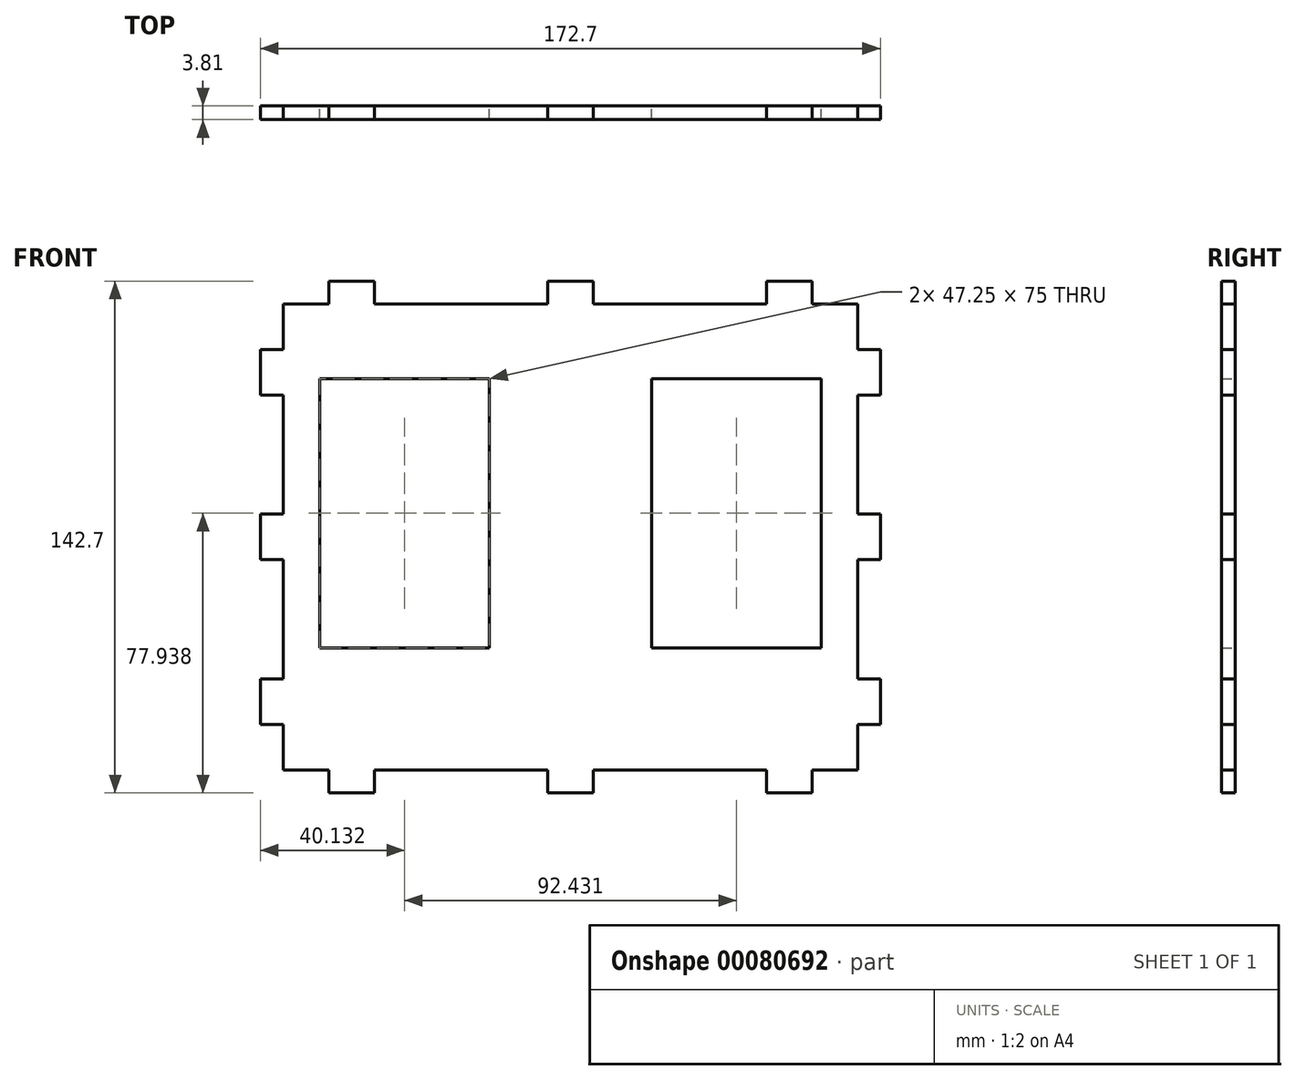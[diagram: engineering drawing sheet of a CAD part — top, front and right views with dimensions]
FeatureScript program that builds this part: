
annotation { "Feature Type Name" : "Feature", "Feature Type Description" : "" }
export const myFeature = defineFeature(function(context is Context, id is Id, definition is map)
    precondition{}
    {
        {
            var Q0;
            Q0=qCreatedBy(makeId("Front.planeOp"),FACE);
            var sketch = newSketch(context, id + "F0", { "sketchPlane" : qUnion([Q0])});
            skLineSegment(sketch, "E0.bottom", {"start": v(-197.85, -61.57) * mm, "end": v(-357.85, -61.57) * mm});
            skLineSegment(sketch, "E0.top", {"start": v(-197.85, 68.43) * mm, "end": v(-357.85, 68.43) * mm});
            skLineSegment(sketch, "E0.left", {"start": v(-197.85, -61.57) * mm, "end": v(-197.85, 68.43) * mm});
            skLineSegment(sketch, "E0.right", {"start": v(-357.85, -61.57) * mm, "end": v(-357.85, 68.43) * mm});
            skPoint(sketch, "E0.middle", {"position": v(-277.85, 3.43) * mm});
            skLineSegment(sketch, "E1.bottom", {"start": v(-271.5, 74.78) * mm, "end": v(-284.2, 74.78) * mm});
            skLineSegment(sketch, "E1.top", {"start": v(-271.5, 62.08) * mm, "end": v(-284.2, 62.08) * mm});
            skLineSegment(sketch, "E1.left", {"start": v(-271.5, 74.78) * mm, "end": v(-271.5, 62.08) * mm});
            skLineSegment(sketch, "E1.right", {"start": v(-284.2, 74.78) * mm, "end": v(-284.2, 62.08) * mm});
            skPoint(sketch, "E1.middle", {"position": v(-277.85, 68.43) * mm});
            skLineSegment(sketch, "E2.bottom", {"start": v(-223.25, 74.78) * mm, "end": v(-210.55, 74.78) * mm});
            skLineSegment(sketch, "E2.top", {"start": v(-223.25, 62.08) * mm, "end": v(-210.55, 62.08) * mm});
            skLineSegment(sketch, "E2.left", {"start": v(-223.25, 74.78) * mm, "end": v(-223.25, 62.08) * mm});
            skLineSegment(sketch, "E2.right", {"start": v(-210.55, 74.78) * mm, "end": v(-210.55, 62.08) * mm});
            skPoint(sketch, "E2.middle", {"position": v(-216.9, 68.43) * mm});
            skLineSegment(sketch, "E3.bottom", {"start": v(-332.45, 74.78) * mm, "end": v(-345.15, 74.78) * mm});
            skLineSegment(sketch, "E3.top", {"start": v(-332.45, 62.08) * mm, "end": v(-345.15, 62.08) * mm});
            skLineSegment(sketch, "E3.left", {"start": v(-332.45, 74.78) * mm, "end": v(-332.45, 62.08) * mm});
            skLineSegment(sketch, "E3.right", {"start": v(-345.15, 74.78) * mm, "end": v(-345.15, 62.08) * mm});
            skPoint(sketch, "E3.middle", {"position": v(-338.8, 68.43) * mm});
            skLineSegment(sketch, "E4.bottom", {"start": v(-364.2, 9.78) * mm, "end": v(-351.5, 9.78) * mm});
            skLineSegment(sketch, "E4.top", {"start": v(-364.2, -2.92) * mm, "end": v(-351.5, -2.92) * mm});
            skLineSegment(sketch, "E4.left", {"start": v(-364.2, 9.78) * mm, "end": v(-364.2, -2.92) * mm});
            skLineSegment(sketch, "E4.right", {"start": v(-351.5, 9.78) * mm, "end": v(-351.5, -2.92) * mm});
            skPoint(sketch, "E4.middle", {"position": v(-357.85, 3.43) * mm});
            skLineSegment(sketch, "E5.bottom", {"start": v(-364.2, 55.73) * mm, "end": v(-351.5, 55.73) * mm});
            skLineSegment(sketch, "E5.top", {"start": v(-364.2, 43.03) * mm, "end": v(-351.5, 43.03) * mm});
            skLineSegment(sketch, "E5.left", {"start": v(-364.2, 55.73) * mm, "end": v(-364.2, 43.03) * mm});
            skLineSegment(sketch, "E5.right", {"start": v(-351.5, 55.73) * mm, "end": v(-351.5, 43.03) * mm});
            skPoint(sketch, "E5.middle", {"position": v(-357.85, 49.38) * mm});
            skLineSegment(sketch, "E6.bottom", {"start": v(-347.7, 47.52) * mm, "end": v(-300.44, 47.52) * mm});
            skLineSegment(sketch, "E6.top", {"start": v(-347.7, -27.48) * mm, "end": v(-300.44, -27.48) * mm});
            skLineSegment(sketch, "E6.left", {"start": v(-347.7, 47.52) * mm, "end": v(-347.7, -27.48) * mm});
            skLineSegment(sketch, "E6.right", {"start": v(-300.44, 47.52) * mm, "end": v(-300.44, -27.48) * mm});
            skLineSegment(sketch, "E7", {"start": v(-277.85, 68.43) * mm, "end": v(-277.85, -61.57) * mm});
            skLineSegment(sketch, "E8.MirrorCS", {"start": v(-255.26, 47.52) * mm, "end": v(-255.26, -27.48) * mm});
            skLineSegment(sketch, "E9.MirrorCS", {"start": v(-208.01, 47.52) * mm, "end": v(-255.26, 47.52) * mm});
            skLineSegment(sketch, "E10.MirrorCS", {"start": v(-208.01, 47.52) * mm, "end": v(-208.01, -27.48) * mm});
            skLineSegment(sketch, "E11.MirrorCS", {"start": v(-208.01, -27.48) * mm, "end": v(-255.26, -27.48) * mm});
            skLineSegment(sketch, "E12.MirrorCS", {"start": v(-271.5, -55.22) * mm, "end": v(-284.2, -55.22) * mm});
            skLineSegment(sketch, "E13.MirrorCS", {"start": v(-284.2, -67.92) * mm, "end": v(-284.2, -55.22) * mm});
            skLineSegment(sketch, "E14.MirrorCS", {"start": v(-271.5, -67.92) * mm, "end": v(-284.2, -67.92) * mm});
            skLineSegment(sketch, "E15.MirrorCS", {"start": v(-271.5, -67.92) * mm, "end": v(-271.5, -55.22) * mm});
            skLineSegment(sketch, "E16.MirrorCS", {"start": v(-223.25, -67.92) * mm, "end": v(-223.25, -55.22) * mm});
            skLineSegment(sketch, "E17.MirrorCS", {"start": v(-223.25, -67.92) * mm, "end": v(-210.55, -67.92) * mm});
            skLineSegment(sketch, "E18.MirrorCS", {"start": v(-210.55, -67.92) * mm, "end": v(-210.55, -55.22) * mm});
            skLineSegment(sketch, "E19.MirrorCS", {"start": v(-223.25, -55.22) * mm, "end": v(-210.55, -55.22) * mm});
            skLineSegment(sketch, "E20.MirrorCS", {"start": v(-332.45, -55.22) * mm, "end": v(-345.15, -55.22) * mm});
            skLineSegment(sketch, "E21.MirrorCS", {"start": v(-332.45, -67.92) * mm, "end": v(-332.45, -55.22) * mm});
            skLineSegment(sketch, "E22.MirrorCS", {"start": v(-332.45, -67.92) * mm, "end": v(-345.15, -67.92) * mm});
            skLineSegment(sketch, "E23.MirrorCS", {"start": v(-345.15, -67.92) * mm, "end": v(-345.15, -55.22) * mm});
            skLineSegment(sketch, "E24.bottom", {"start": v(-364.2, -36.17) * mm, "end": v(-351.5, -36.17) * mm});
            skLineSegment(sketch, "E24.top", {"start": v(-364.2, -48.87) * mm, "end": v(-351.5, -48.87) * mm});
            skLineSegment(sketch, "E24.left", {"start": v(-364.2, -36.17) * mm, "end": v(-364.2, -48.87) * mm});
            skLineSegment(sketch, "E24.right", {"start": v(-351.5, -36.17) * mm, "end": v(-351.5, -48.87) * mm});
            skPoint(sketch, "E24.middle", {"position": v(-357.85, -42.52) * mm});
            skLineSegment(sketch, "E25.MirrorCS", {"start": v(-204.2, -36.17) * mm, "end": v(-204.2, -48.87) * mm});
            skLineSegment(sketch, "E26.MirrorCS", {"start": v(-191.5, -36.17) * mm, "end": v(-204.2, -36.17) * mm});
            skLineSegment(sketch, "E27.MirrorCS", {"start": v(-191.5, -36.17) * mm, "end": v(-191.5, -48.87) * mm});
            skLineSegment(sketch, "E28.MirrorCS", {"start": v(-191.5, -48.87) * mm, "end": v(-204.2, -48.87) * mm});
            skLineSegment(sketch, "E29.MirrorCS", {"start": v(-191.5, -2.92) * mm, "end": v(-204.2, -2.92) * mm});
            skLineSegment(sketch, "E30.MirrorCS", {"start": v(-204.2, 9.78) * mm, "end": v(-204.2, -2.92) * mm});
            skLineSegment(sketch, "E31.MirrorCS", {"start": v(-191.5, 9.78) * mm, "end": v(-204.2, 9.78) * mm});
            skLineSegment(sketch, "E32.MirrorCS", {"start": v(-191.5, 9.78) * mm, "end": v(-191.5, -2.92) * mm});
            skLineSegment(sketch, "E33.MirrorCS", {"start": v(-191.5, 43.03) * mm, "end": v(-204.2, 43.03) * mm});
            skLineSegment(sketch, "E34.MirrorCS", {"start": v(-191.5, 55.73) * mm, "end": v(-204.2, 55.73) * mm});
            skLineSegment(sketch, "E35.MirrorCS", {"start": v(-204.2, 55.73) * mm, "end": v(-204.2, 43.03) * mm});
            skLineSegment(sketch, "E36.MirrorCS", {"start": v(-191.5, 55.73) * mm, "end": v(-191.5, 43.03) * mm});
            skPoint(sketch, "E37.trimOffspring.end.orphan", {"position": v(-197.85, 3.43) * mm});
            skSolve(sketch);
        }
        {
            var Q0;
            {var subQ5=sQuery(id+"F0.wireOp",EDGE,"E5.right");Q0=makeQuery(id+"F0.imprint","IMPRINT",FACE,{"disambiguationData":[TD([[makeQuery(id+"F0.imprint","IMPRINT",EDGE,{"derivedFrom":subQ5}),-1.0]])]});}
            var Q1;
            {var subQ5=sQuery(id+"F0.wireOp",EDGE,"E5.left");Q1=makeQuery(id+"F0.imprint","IMPRINT",FACE,{"disambiguationData":[TD([[makeQuery(id+"F0.imprint","IMPRINT",EDGE,{"derivedFrom":subQ5}),1.0]])]});}
            var Q2;
            {var subQ0=sQuery(id+"F0.wireOp",EDGE,"E0.right");var subQ1=sQuery(id+"F0.wireOp",EDGE,"E0.top");var subQ2=makeQuery(id+"F0.imprint","INTERSECT",VERTEX,{"derivedFrom":[subQ1,subQ0]});Q2=makeQuery(id+"F0.imprint","IMPRINT",FACE,{"disambiguationData":[TD([[makeQuery(id+"F0.imprint","IMPRINT",EDGE,{"disambiguationData":[TD([[subQ2,1.0]])],"derivedFrom":subQ1}),1.0]])]});}
            var Q3;
            {var subQ5=sQuery(id+"F0.wireOp",EDGE,"E3.top");Q3=makeQuery(id+"F0.imprint","IMPRINT",FACE,{"disambiguationData":[TD([[makeQuery(id+"F0.imprint","IMPRINT",EDGE,{"derivedFrom":subQ5}),-1.0]])]});}
            var Q4;
            {var subQ5=sQuery(id+"F0.wireOp",EDGE,"E3.bottom");Q4=makeQuery(id+"F0.imprint","IMPRINT",FACE,{"disambiguationData":[TD([[makeQuery(id+"F0.imprint","IMPRINT",EDGE,{"derivedFrom":subQ5}),1.0]])]});}
            var Q5;
            {var subQ31=sQuery(id+"F0.wireOp",EDGE,"E1.top");Q5=makeQuery(id+"F0.imprint","IMPRINT",FACE,{"disambiguationData":[TD([[makeQuery(id+"F0.imprint","IMPRINT",EDGE,{"derivedFrom":subQ31}),1.0]])]});}
            var Q6;
            {var subQ5=sQuery(id+"F0.wireOp",EDGE,"E1.bottom");Q6=makeQuery(id+"F0.imprint","IMPRINT",FACE,{"disambiguationData":[TD([[makeQuery(id+"F0.imprint","IMPRINT",EDGE,{"derivedFrom":subQ5}),1.0]])]});}
            var Q7;
            {var subQ5=sQuery(id+"F0.wireOp",EDGE,"E1.top");Q7=makeQuery(id+"F0.imprint","IMPRINT",FACE,{"disambiguationData":[TD([[makeQuery(id+"F0.imprint","IMPRINT",EDGE,{"derivedFrom":subQ5}),-1.0]])]});}
            var Q8;
            {var subQ5=sQuery(id+"F0.wireOp",EDGE,"E2.bottom");Q8=makeQuery(id+"F0.imprint","IMPRINT",FACE,{"disambiguationData":[TD([[makeQuery(id+"F0.imprint","IMPRINT",EDGE,{"derivedFrom":subQ5}),-1.0]])]});}
            var Q9;
            {var subQ5=sQuery(id+"F0.wireOp",EDGE,"E2.top");Q9=makeQuery(id+"F0.imprint","IMPRINT",FACE,{"disambiguationData":[TD([[makeQuery(id+"F0.imprint","IMPRINT",EDGE,{"derivedFrom":subQ5}),1.0]])]});}
            var Q10;
            {var subQ0=sQuery(id+"F0.wireOp",EDGE,"E0.left");var subQ1=sQuery(id+"F0.wireOp",EDGE,"E0.top");var subQ2=makeQuery(id+"F0.imprint","INTERSECT",VERTEX,{"derivedFrom":[subQ1,subQ0]});Q10=makeQuery(id+"F0.imprint","IMPRINT",FACE,{"disambiguationData":[TD([[makeQuery(id+"F0.imprint","IMPRINT",EDGE,{"disambiguationData":[TD([[subQ2,-1.0]])],"derivedFrom":subQ1}),1.0]])]});}
            var Q11;
            {var subQ5=sQuery(id+"F0.wireOp",EDGE,"6e67ea2a-bf6c-4d8d-991e-4c9610f454840.MirrorCS");Q11=makeQuery(id+"F0.imprint","IMPRINT",FACE,{"disambiguationData":[TD([[makeQuery(id+"F0.imprint","IMPRINT",EDGE,{"derivedFrom":subQ5}),1.0]])]});}
            var Q12;
            {var subQ5=sQuery(id+"F0.wireOp",EDGE,"e7a02cae-3dec-4235-90d6-44147ae123860.MirrorCS");Q12=makeQuery(id+"F0.imprint","IMPRINT",FACE,{"disambiguationData":[TD([[makeQuery(id+"F0.imprint","IMPRINT",EDGE,{"derivedFrom":subQ5}),-1.0]])]});}
            var Q13;
            {var subQ5=sQuery(id+"F0.wireOp",EDGE,"b77bcf1b-6ed8-48e8-9d4e-b293c0d97bf70.MirrorCS");Q13=makeQuery(id+"F0.imprint","IMPRINT",FACE,{"disambiguationData":[TD([[makeQuery(id+"F0.imprint","IMPRINT",EDGE,{"derivedFrom":subQ5}),1.0]])]});}
            var Q14;
            {var subQ5=sQuery(id+"F0.wireOp",EDGE,"3d584175-bd42-42f6-9b5a-85d0e25869fe0.MirrorCS");Q14=makeQuery(id+"F0.imprint","IMPRINT",FACE,{"disambiguationData":[TD([[makeQuery(id+"F0.imprint","IMPRINT",EDGE,{"derivedFrom":subQ5}),-1.0]])]});}
            var Q15;
            {var subQ5=sQuery(id+"F0.wireOp",EDGE,"cdb6775e-2d37-4d6a-90fa-4eca167a4fed0.MirrorCS");Q15=makeQuery(id+"F0.imprint","IMPRINT",FACE,{"disambiguationData":[TD([[makeQuery(id+"F0.imprint","IMPRINT",EDGE,{"derivedFrom":subQ5}),1.0]])]});}
            var Q16;
            {var subQ5=sQuery(id+"F0.wireOp",EDGE,"1e18de7c-31cb-43aa-ab19-022ff6750b660.MirrorCS");Q16=makeQuery(id+"F0.imprint","IMPRINT",FACE,{"disambiguationData":[TD([[makeQuery(id+"F0.imprint","IMPRINT",EDGE,{"derivedFrom":subQ5}),-1.0]])]});}
            var Q17;
            {var subQ0=sQuery(id+"F0.wireOp",EDGE,"38f30ffd-d7d7-4048-a385-bb1ef51f31f00.MirrorCS");var subQ1=sQuery(id+"F0.wireOp",EDGE,"E0.left");var subQ2=makeQuery(id+"F0.imprint","INTERSECT",VERTEX,{"derivedFrom":[subQ1,subQ0]});Q17=makeQuery(id+"F0.imprint","IMPRINT",FACE,{"disambiguationData":[TD([[makeQuery(id+"F0.imprint","IMPRINT",EDGE,{"disambiguationData":[TD([[subQ2,-1.0]])],"derivedFrom":subQ1}),1.0]])]});}
            var Q18;
            {var subQ5=sQuery(id+"F0.wireOp",EDGE,"8c4a78ce-fe7b-4a0c-9cb1-67b932f80da20.MirrorCS");Q18=makeQuery(id+"F0.imprint","IMPRINT",FACE,{"disambiguationData":[TD([[makeQuery(id+"F0.imprint","IMPRINT",EDGE,{"derivedFrom":subQ5}),-1.0]])]});}
            var Q19;
            {var subQ5=sQuery(id+"F0.wireOp",EDGE,"665f2488-0e6a-4b9e-9c0d-889857a463930.MirrorCS");Q19=makeQuery(id+"F0.imprint","IMPRINT",FACE,{"disambiguationData":[TD([[makeQuery(id+"F0.imprint","IMPRINT",EDGE,{"derivedFrom":subQ5}),1.0]])]});}
            var Q20;
            {var subQ5=sQuery(id+"F0.wireOp",EDGE,"7cdf0428-d974-4590-92a7-2ffb3f6deecd0.MirrorCS");Q20=makeQuery(id+"F0.imprint","IMPRINT",FACE,{"disambiguationData":[TD([[makeQuery(id+"F0.imprint","IMPRINT",EDGE,{"derivedFrom":subQ5}),1.0]])]});}
            var Q21;
            {var subQ5=sQuery(id+"F0.wireOp",EDGE,"a4e31e00-16c8-444c-b41a-9d1313db8a300.MirrorCS");Q21=makeQuery(id+"F0.imprint","IMPRINT",FACE,{"disambiguationData":[TD([[makeQuery(id+"F0.imprint","IMPRINT",EDGE,{"derivedFrom":subQ5}),-1.0]])]});}
            var Q22;
            {var subQ0=sQuery(id+"F0.wireOp",EDGE,"23c010f1-1732-4b4f-a1bf-fdb20c1cfe8f0.MirrorCS");Q22=makeQuery(id+"F0.imprint","IMPRINT",FACE,{"disambiguationData":[TD([[makeQuery(id+"F0.imprint","IMPRINT",EDGE,{"derivedFrom":subQ0}),1.0]])]});}
            var Q23;
            {var subQ0=sQuery(id+"F0.wireOp",EDGE,"1db746d3-bed4-4ef7-9f53-c32ba9d8edd40.MirrorCS");Q23=makeQuery(id+"F0.imprint","IMPRINT",FACE,{"disambiguationData":[TD([[makeQuery(id+"F0.imprint","IMPRINT",EDGE,{"derivedFrom":subQ0}),-1.0]])]});}
            var Q24;
            {var subQ0=sQuery(id+"F0.wireOp",EDGE,"38f30ffd-d7d7-4048-a385-bb1ef51f31f00.MirrorCS");var subQ1=sQuery(id+"F0.wireOp",EDGE,"E0.right");var subQ2=makeQuery(id+"F0.imprint","INTERSECT",VERTEX,{"derivedFrom":[subQ1,subQ0]});Q24=makeQuery(id+"F0.imprint","IMPRINT",FACE,{"disambiguationData":[TD([[makeQuery(id+"F0.imprint","IMPRINT",EDGE,{"disambiguationData":[TD([[subQ2,-1.0]])],"derivedFrom":subQ1}),-1.0]])]});}
            var Q25;
            {var subQ5=sQuery(id+"F0.wireOp",EDGE,"631de5aa-dca1-49e2-99dd-c5ba14d8356f0.MirrorCS");Q25=makeQuery(id+"F0.imprint","IMPRINT",FACE,{"disambiguationData":[TD([[makeQuery(id+"F0.imprint","IMPRINT",EDGE,{"derivedFrom":subQ5}),1.0]])]});}
            var Q26;
            {var subQ5=sQuery(id+"F0.wireOp",EDGE,"4b58c554-b021-4d2c-8e63-d08e2fe331a00.MirrorCS");Q26=makeQuery(id+"F0.imprint","IMPRINT",FACE,{"disambiguationData":[TD([[makeQuery(id+"F0.imprint","IMPRINT",EDGE,{"derivedFrom":subQ5}),-1.0]])]});}
            var Q27;
            {var subQ5=sQuery(id+"F0.wireOp",EDGE,"E4.right");Q27=makeQuery(id+"F0.imprint","IMPRINT",FACE,{"disambiguationData":[TD([[makeQuery(id+"F0.imprint","IMPRINT",EDGE,{"derivedFrom":subQ5}),-1.0]])]});}
            var Q28;
            {var subQ5=sQuery(id+"F0.wireOp",EDGE,"E4.left");Q28=makeQuery(id+"F0.imprint","IMPRINT",FACE,{"disambiguationData":[TD([[makeQuery(id+"F0.imprint","IMPRINT",EDGE,{"derivedFrom":subQ5}),1.0]])]});}
            var Q29;
            {var subQ5=sQuery(id+"F0.wireOp",EDGE,"70ba0a8e-15ca-4af5-ad1e-aec15cda82ba0.MirrorCS");Q29=makeQuery(id+"F0.imprint","IMPRINT",FACE,{"disambiguationData":[TD([[makeQuery(id+"F0.imprint","IMPRINT",EDGE,{"derivedFrom":subQ5}),1.0]])]});}
            var Q30;
            {var subQ5=sQuery(id+"F0.wireOp",EDGE,"05116e00-459e-4e34-ad64-0683ffe88f100.MirrorCS");Q30=makeQuery(id+"F0.imprint","IMPRINT",FACE,{"disambiguationData":[TD([[makeQuery(id+"F0.imprint","IMPRINT",EDGE,{"derivedFrom":subQ5}),-1.0]])]});}
            var Q31;
            {var subQ5=sQuery(id+"F0.wireOp",EDGE,"6eea4c6f-bbe4-46e0-a570-8c34d712b9610.MirrorCS");Q31=makeQuery(id+"F0.imprint","IMPRINT",FACE,{"disambiguationData":[TD([[makeQuery(id+"F0.imprint","IMPRINT",EDGE,{"derivedFrom":subQ5}),-1.0]])]});}
            var Q32;
            {var subQ5=sQuery(id+"F0.wireOp",EDGE,"f1c2bbc9-7080-4b4f-8636-39eca44de4050.MirrorCS");Q32=makeQuery(id+"F0.imprint","IMPRINT",FACE,{"disambiguationData":[TD([[makeQuery(id+"F0.imprint","IMPRINT",EDGE,{"derivedFrom":subQ5}),1.0]])]});}
            var Q33;
            {var subQ5=sQuery(id+"F0.wireOp",EDGE,"E24.left");Q33=makeQuery(id+"F0.imprint","IMPRINT",FACE,{"disambiguationData":[TD([[makeQuery(id+"F0.imprint","IMPRINT",EDGE,{"derivedFrom":subQ5}),1.0]])]});}
            var Q34;
            {var subQ5=sQuery(id+"F0.wireOp",EDGE,"E22.MirrorCS");Q34=makeQuery(id+"F0.imprint","IMPRINT",FACE,{"disambiguationData":[TD([[makeQuery(id+"F0.imprint","IMPRINT",EDGE,{"derivedFrom":subQ5}),-1.0]])]});}
            var Q35;
            {var subQ5=sQuery(id+"F0.wireOp",EDGE,"E24.right");Q35=makeQuery(id+"F0.imprint","IMPRINT",FACE,{"disambiguationData":[TD([[makeQuery(id+"F0.imprint","IMPRINT",EDGE,{"derivedFrom":subQ5}),-1.0]])]});}
            var Q36;
            {var subQ5=sQuery(id+"F0.wireOp",EDGE,"E20.MirrorCS");Q36=makeQuery(id+"F0.imprint","IMPRINT",FACE,{"disambiguationData":[TD([[makeQuery(id+"F0.imprint","IMPRINT",EDGE,{"derivedFrom":subQ5}),1.0]])]});}
            var Q37;
            {var subQ0=sQuery(id+"F0.wireOp",EDGE,"E7");var subQ1=sQuery(id+"F0.wireOp",EDGE,"E0.bottom");var subQ2=makeQuery(id+"F0.imprint","INTERSECT",VERTEX,{"derivedFrom":[subQ1,subQ0]});Q37=makeQuery(id+"F0.imprint","IMPRINT",FACE,{"disambiguationData":[TD([[makeQuery(id+"F0.imprint","IMPRINT",EDGE,{"disambiguationData":[TD([[subQ2,-1.0]])],"derivedFrom":subQ1}),-1.0]])]});}
            var Q38;
            {var subQ0=sQuery(id+"F0.wireOp",EDGE,"E7");var subQ1=sQuery(id+"F0.wireOp",EDGE,"E0.bottom");var subQ2=makeQuery(id+"F0.imprint","INTERSECT",VERTEX,{"derivedFrom":[subQ1,subQ0]});Q38=makeQuery(id+"F0.imprint","IMPRINT",FACE,{"disambiguationData":[TD([[makeQuery(id+"F0.imprint","IMPRINT",EDGE,{"disambiguationData":[TD([[subQ2,1.0]])],"derivedFrom":subQ1}),-1.0]])]});}
            var Q39;
            {var subQ0=sQuery(id+"F0.wireOp",EDGE,"E14.MirrorCS");Q39=makeQuery(id+"F0.imprint","IMPRINT",FACE,{"disambiguationData":[TD([[makeQuery(id+"F0.imprint","IMPRINT",EDGE,{"derivedFrom":subQ0}),-1.0]])]});}
            var Q40;
            {var subQ5=sQuery(id+"F0.wireOp",EDGE,"E17.MirrorCS");Q40=makeQuery(id+"F0.imprint","IMPRINT",FACE,{"disambiguationData":[TD([[makeQuery(id+"F0.imprint","IMPRINT",EDGE,{"derivedFrom":subQ5}),1.0]])]});}
            var Q41;
            {var subQ5=sQuery(id+"F0.wireOp",EDGE,"E19.MirrorCS");Q41=makeQuery(id+"F0.imprint","IMPRINT",FACE,{"disambiguationData":[TD([[makeQuery(id+"F0.imprint","IMPRINT",EDGE,{"derivedFrom":subQ5}),-1.0]])]});}
            var Q42;
            {var subQ5=sQuery(id+"F0.wireOp",EDGE,"E25.MirrorCS");Q42=makeQuery(id+"F0.imprint","IMPRINT",FACE,{"disambiguationData":[TD([[makeQuery(id+"F0.imprint","IMPRINT",EDGE,{"derivedFrom":subQ5}),1.0]])]});}
            var Q43;
            {var subQ5=sQuery(id+"F0.wireOp",EDGE,"E27.MirrorCS");Q43=makeQuery(id+"F0.imprint","IMPRINT",FACE,{"disambiguationData":[TD([[makeQuery(id+"F0.imprint","IMPRINT",EDGE,{"derivedFrom":subQ5}),-1.0]])]});}
            var Q44;
            {var subQ5=sQuery(id+"F0.wireOp",EDGE,"E30.MirrorCS");Q44=makeQuery(id+"F0.imprint","IMPRINT",FACE,{"disambiguationData":[TD([[makeQuery(id+"F0.imprint","IMPRINT",EDGE,{"derivedFrom":subQ5}),1.0]])]});}
            var Q45;
            {var subQ5=sQuery(id+"F0.wireOp",EDGE,"E32.MirrorCS");Q45=makeQuery(id+"F0.imprint","IMPRINT",FACE,{"disambiguationData":[TD([[makeQuery(id+"F0.imprint","IMPRINT",EDGE,{"derivedFrom":subQ5}),-1.0]])]});}
            var Q46;
            {var subQ5=sQuery(id+"F0.wireOp",EDGE,"E35.MirrorCS");Q46=makeQuery(id+"F0.imprint","IMPRINT",FACE,{"disambiguationData":[TD([[makeQuery(id+"F0.imprint","IMPRINT",EDGE,{"derivedFrom":subQ5}),1.0]])]});}
            var Q47;
            {var subQ5=sQuery(id+"F0.wireOp",EDGE,"E36.MirrorCS");Q47=makeQuery(id+"F0.imprint","IMPRINT",FACE,{"disambiguationData":[TD([[makeQuery(id+"F0.imprint","IMPRINT",EDGE,{"derivedFrom":subQ5}),-1.0]])]});}
            extrude(context, id + "F1", {"entities" : qUnion([Q0, Q1, Q2, Q3, Q4, Q5, Q6, Q7, Q8, Q9, Q10, Q11, Q12, Q13, Q14, Q15, Q16, Q17, Q18, Q19, Q20, Q21, Q22, Q23, Q24, Q25, Q26, Q27, Q28, Q29, Q30, Q31, Q32, Q33, Q34, Q35, Q36, Q37, Q38, Q39, Q40, Q41, Q42, Q43, Q44, Q45, Q46, Q47]), "depth" : 3.8 * mm});
        }
    });
